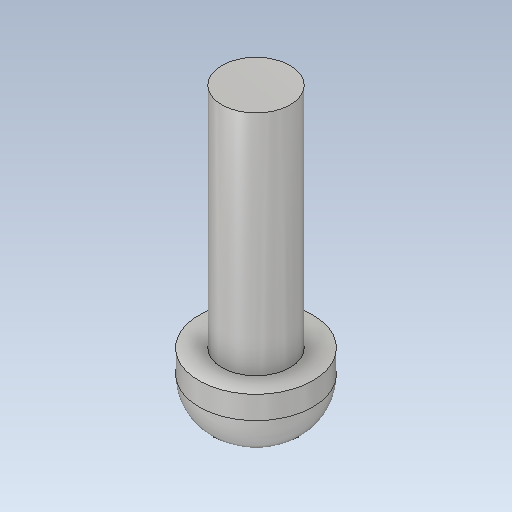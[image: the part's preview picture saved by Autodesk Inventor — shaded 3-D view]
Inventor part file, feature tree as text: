
AUTODESK INVENTOR PART (.ipt)
format: ipt  version: 2020 (Build 240168000, 168)  size: 166,912 bytes
history: native  units: mm
features: extrude x4, sketch x4, projected_geometry x2, fillet x1, mirror x1, pattern_circular x1
ambient origin geometry x8: Origin, YZ Plane, XZ Plane, XY Plane, X Axis, Y Axis, Z Axis, Center Point
bodies: Solid1 (feature_tree)
feature tree (13):
  extrude  "Extrusion1"  Depth=10.0mm TaperAngle=0.0deg
  extrude  "Extrusion2"  Depth=3.0mm TaperAngle=0.0deg
  fillet  "Fillet1"  Radius=2.0mm
  extrude  "Extrusion3"  TaperAngle=0.0deg  [1 undecoded]
  mirror  "Mirror1"
  pattern_circular  "Circular Pattern1"  Count=4 Angle=360.0deg
  extrude  "Extrusion4"  [1 undecoded]
  sketch  "Sketch1"  dims[d0=3.0mm d1=10.0mm d2=0.0mm]
  sketch  "Sketch2"  dims[d3=5.0mm d4=3.0mm d5=0.0mm d6=2.0mm]
  sketch  "Sketch3"  dims[d7=2.0mm d8=0.0mm d9=0.0mm d10=40.0mm d11=360.0deg]
  projected_geometry  "Projected Loop1"
  sketch  "Sketch4"  dims[d13=2.0mm d14=0.0mm]
  projected_geometry  "Projected Loop2"
note: 2 required parameter values undecoded (feature->parameter linkage not recoverable at this tier; creation-order binding heuristic only, values carry confidence <= 0.55)
